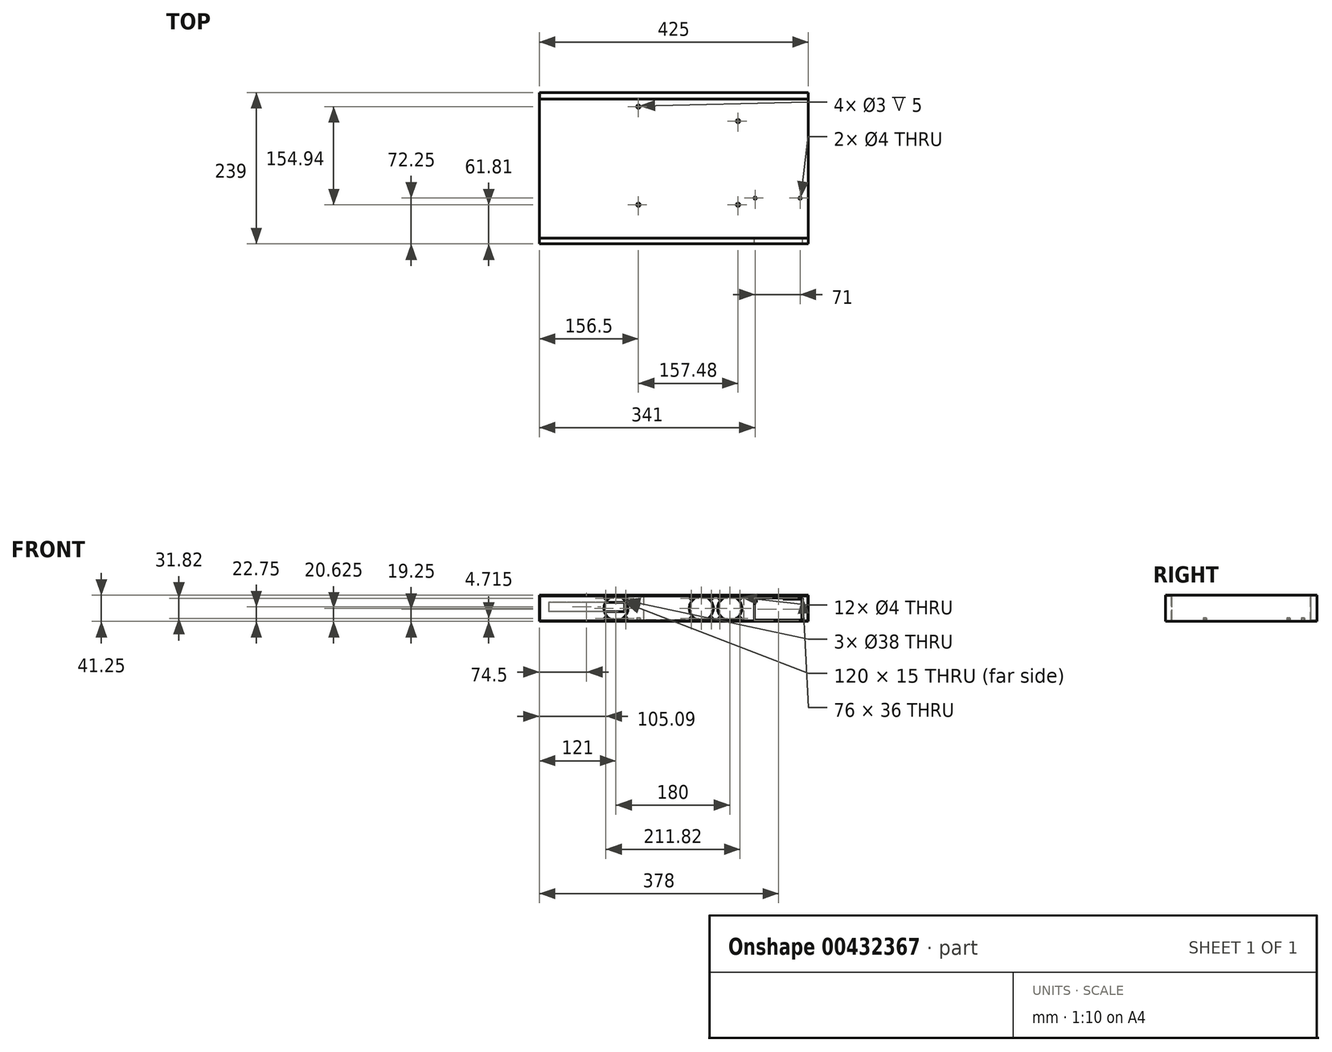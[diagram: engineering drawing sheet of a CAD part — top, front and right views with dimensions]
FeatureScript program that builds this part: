
annotation { "Feature Type Name" : "Feature", "Feature Type Description" : "" }
export const myFeature = defineFeature(function(context is Context, id is Id, definition is map)
    precondition{}
    {
        {
            var Q0;
            Q0=qCreatedBy(makeId("Top.planeOp"),FACE);
            var sketch = newSketch(context, id + "F0", { "sketchPlane" : qUnion([Q0])});
            skLineSegment(sketch, "E0.bottom", {"start": v(0, 219.75) * mm, "end": v(424.5, 219.75) * mm});
            skLineSegment(sketch, "E0.top", {"start": v(0, 0.25) * mm, "end": v(424.5, 0.25) * mm});
            skLineSegment(sketch, "E0.left", {"start": v(0, 219.75) * mm, "end": v(0, 0.25) * mm});
            skLineSegment(sketch, "E0.right", {"start": v(424.5, 219.75) * mm, "end": v(424.5, 0.25) * mm});
            skLineSegment(sketch, "E1.0", {"start": v(-0.25, 220) * mm, "end": v(-0.25, 0) * mm});
            skLineSegment(sketch, "E1.1", {"start": v(-0.25, 220) * mm, "end": v(424.75, 220) * mm});
            skLineSegment(sketch, "E1.2", {"start": v(424.75, 220) * mm, "end": v(424.75, 0) * mm});
            skLineSegment(sketch, "E1.3", {"start": v(-0.25, 0) * mm, "end": v(424.75, 0) * mm});
            skSolve(sketch);
        }
        {
            var Q0;
            Q0=makeQuery(id+"F0.imprint","IMPRINT",FACE,{"disambiguationData":[TD([[makeQuery(id+"F0.imprint","IMPRINT",EDGE,{"derivedFrom":sQuery(id+"F0.wireOp",EDGE,"E0.bottom")}),-1.0]])]});
            var Q1;
            Q1=makeQuery(id+"F0.imprint","IMPRINT",FACE,{"disambiguationData":[TD([[makeQuery(id+"F0.imprint","IMPRINT",EDGE,{"derivedFrom":sQuery(id+"F0.wireOp",EDGE,"E0.bottom")}),1.0]])]});
            extrude(context, id + "F1", {"entities" : qUnion([Q0, Q1]), "oppositeDirection" : true, "depth" : .25 * mm});
        }
        {
            var Q0;
            Q0 = qSketchRegion(id + "F0", true);
            extrude(context, id + "F2", {"entities" : qUnion([Q0]), "operationType" : NewBodyOperationType.ADD, "depth" : 41 * mm});
        }
        {
            var Q0;
            {var subQ0=sQuery(id+"F0.wireOp",EDGE,"E1.3");Q0=makeQuery(id+"F2.boolean.opBoolean","MERGE",FACE,{"derivedFrom":[makeQuery(id+"F1.opExtrude","SWEPT_FACE",FACE,{"disambiguationData":[OSD([subQ0])]}),makeQuery(id+"F2.opExtrude","SWEPT_FACE",FACE,{"disambiguationData":[OSD([subQ0])]})]});}
            var sketch = newSketch(context, id + "F3", { "sketchPlane" : qUnion([Q0])});
            skLineSegment(sketch, "E2", {"start": v(-0.25, 20.37) * mm, "end": v(424.75, 20.38) * mm, "construction": true});
            skCircle(sketch, "E3", {"center": v(120.75, 20.38) * mm, "radius": 19 * mm});
            skCircle(sketch, "E4", {"center": v(255.75, 20.38) * mm, "radius": 19 * mm});
            skCircle(sketch, "E5", {"center": v(300.75, 20.38) * mm, "radius": 19 * mm});
            skLineSegment(sketch, "E6.bottom", {"start": v(339.75, 37) * mm, "end": v(415.75, 37) * mm});
            skLineSegment(sketch, "E6.top", {"start": v(339.75, 1) * mm, "end": v(415.75, 1) * mm});
            skLineSegment(sketch, "E6.left", {"start": v(339.75, 37) * mm, "end": v(339.75, 1) * mm});
            skLineSegment(sketch, "E6.right", {"start": v(415.75, 37) * mm, "end": v(415.75, 1) * mm});
            skCircle(sketch, "E7", {"center": v(104.84, 36.28) * mm, "radius": 2 * mm});
            skLineSegment(sketch, "E8", {"start": v(188.25, 41) * mm, "end": v(188.25, 0) * mm, "construction": true});
            skLineSegment(sketch, "E9", {"start": v(278.25, 41) * mm, "end": v(278.25, 0) * mm, "construction": true});
            skLineSegment(sketch, "E10", {"start": v(104.84, 36.28) * mm, "end": v(120.75, 20.38) * mm, "construction": true});
            skCircle(sketch, "E11.MirrorC", {"center": v(104.84, 4.47) * mm, "radius": 2 * mm});
            skCircle(sketch, "E12.MirrorC", {"center": v(271.66, 36.28) * mm, "radius": 2 * mm});
            skCircle(sketch, "E13.MirrorC", {"center": v(271.66, 4.47) * mm, "radius": 2 * mm});
            skLineSegment(sketch, "E14", {"start": v(120.75, 20.38) * mm, "end": v(120.75, 39.38) * mm, "construction": true});
            skCircle(sketch, "E15.MirrorC", {"center": v(136.66, 36.28) * mm, "radius": 2 * mm});
            skCircle(sketch, "E16.MirrorC", {"center": v(136.66, 4.47) * mm, "radius": 2 * mm});
            skCircle(sketch, "E17.MirrorC", {"center": v(239.84, 36.28) * mm, "radius": 2 * mm});
            skCircle(sketch, "E18.MirrorC", {"center": v(239.84, 4.47) * mm, "radius": 2 * mm});
            skCircle(sketch, "E19.MirrorC", {"center": v(284.84, 36.28) * mm, "radius": 2 * mm});
            skCircle(sketch, "E20.MirrorC", {"center": v(284.84, 4.47) * mm, "radius": 2 * mm});
            skCircle(sketch, "E21.MirrorC", {"center": v(316.66, 36.28) * mm, "radius": 2 * mm});
            skCircle(sketch, "E22.MirrorC", {"center": v(316.66, 4.47) * mm, "radius": 2 * mm});
            skSolve(sketch);
        }
        {
            var Q0;
            {var subQ0=sQuery(id+"F0.wireOp",EDGE,"E1.1");Q0=makeQuery(id+"F2.boolean.opBoolean","MERGE",FACE,{"derivedFrom":[makeQuery(id+"F1.opExtrude","SWEPT_FACE",FACE,{"disambiguationData":[OSD([subQ0])]}),makeQuery(id+"F2.opExtrude","SWEPT_FACE",FACE,{"disambiguationData":[OSD([subQ0])]})]});}
            var sketch = newSketch(context, id + "F4", { "sketchPlane" : qUnion([Q0])});
            skLineSegment(sketch, "E23", {"start": v(-424.75, 20.37) * mm, "end": v(0.25, 20.38) * mm, "construction": true});
            skLineSegment(sketch, "E24.bottom", {"start": v(-414.75, 34.75) * mm, "end": v(-384.75, 34.75) * mm});
            skLineSegment(sketch, "E24.top", {"start": v(-414.75, 1.75) * mm, "end": v(-338.75, 1.75) * mm});
            skLineSegment(sketch, "E24.left", {"start": v(-414.75, 34.75) * mm, "end": v(-414.75, 1.75) * mm});
            skLineSegment(sketch, "E24.right", {"start": v(-338.75, 30) * mm, "end": v(-338.75, 1.75) * mm});
            skLineSegment(sketch, "E25.bottom", {"start": v(-322.25, 40) * mm, "end": v(-164.25, 40) * mm});
            skLineSegment(sketch, "E25.top", {"start": v(-322.25, 1.75) * mm, "end": v(-164.25, 1.75) * mm});
            skLineSegment(sketch, "E25.left", {"start": v(-322.25, 40) * mm, "end": v(-322.25, 1.75) * mm});
            skLineSegment(sketch, "E25.right", {"start": v(-164.25, 40) * mm, "end": v(-164.25, 1.75) * mm});
            skLineSegment(sketch, "E26.bottom", {"start": v(-134.25, 30) * mm, "end": v(-14.25, 30) * mm});
            skLineSegment(sketch, "E26.top", {"start": v(-134.25, 15) * mm, "end": v(-14.25, 15) * mm});
            skLineSegment(sketch, "E26.left", {"start": v(-134.25, 30) * mm, "end": v(-134.25, 15) * mm});
            skLineSegment(sketch, "E26.right", {"start": v(-14.25, 30) * mm, "end": v(-14.25, 15) * mm});
            skLineSegment(sketch, "E27.bottom", {"start": v(-384.75, 40) * mm, "end": v(-342.75, 40) * mm});
            skLineSegment(sketch, "E27.left", {"start": v(-384.75, 40) * mm, "end": v(-384.75, 34.75) * mm});
            skLineSegment(sketch, "E27.right", {"start": v(-342.75, 40) * mm, "end": v(-342.75, 40) * mm});
            skLineSegment(sketch, "E28.top", {"start": v(-342.75, 30) * mm, "end": v(-338.75, 30) * mm});
            skLineSegment(sketch, "E28.left", {"start": v(-342.75, 40) * mm, "end": v(-342.75, 30) * mm});
            skSolve(sketch);
        }
        {
            var Q0;
            Q0 = qSketchRegion(id + "F3", true);
            extrude(context, id + "F5", {"entities" : qUnion([Q0]), "operationType" : NewBodyOperationType.REMOVE, "oppositeDirection" : true, "depth" : 1 * mm});
        }
        {
            var Q0;
            Q0 = qSketchRegion(id + "F4", true);
            extrude(context, id + "F6", {"entities" : qUnion([Q0]), "operationType" : NewBodyOperationType.REMOVE, "oppositeDirection" : true, "depth" : 1 * mm});
        }
        {
            var Q0;
            {var subQ0=sQuery(id+"F0.wireOp",EDGE,"E1.3");Q0=makeQuery(id+"F2.boolean.opBoolean","MERGE",FACE,{"derivedFrom":[makeQuery(id+"F1.opExtrude","SWEPT_FACE",FACE,{"disambiguationData":[OSD([subQ0])]}),makeQuery(id+"F2.opExtrude","SWEPT_FACE",FACE,{"disambiguationData":[OSD([subQ0])]})]});}
            var sketch = newSketch(context, id + "F7", { "sketchPlane" : qUnion([Q0])});
            skLineSegment(sketch, "E29.bottom", {"start": v(-0.25, 41) * mm, "end": v(424.75, 41) * mm});
            skLineSegment(sketch, "E29.top", {"start": v(-0.25, -0.25) * mm, "end": v(339.75, -0.25) * mm});
            skLineSegment(sketch, "E29.left", {"start": v(-0.25, 41) * mm, "end": v(-0.25, -0.25) * mm});
            skLineSegment(sketch, "E29.right", {"start": v(424.75, 41) * mm, "end": v(424.75, -0.25) * mm});
            skLineSegment(sketch, "E30.0", {"start": v(0.75, 40) * mm, "end": v(0.75, 0.75) * mm});
            skLineSegment(sketch, "E30.1", {"start": v(0.75, 40) * mm, "end": v(423.75, 40) * mm});
            skLineSegment(sketch, "E30.2", {"start": v(423.75, 40) * mm, "end": v(423.75, 0.75) * mm});
            skLineSegment(sketch, "E30.3", {"start": v(0.75, 0.75) * mm, "end": v(339.75, 0.75) * mm});
            skLineSegment(sketch, "E31", {"start": v(339.75, 0.75) * mm, "end": v(339.75, -0.25) * mm});
            skLineSegment(sketch, "E32", {"start": v(415.75, 0.75) * mm, "end": v(415.75, -0.25) * mm});
            skLineSegment(sketch, "E33.trimOffspring", {"start": v(415.75, 0.75) * mm, "end": v(423.75, 0.75) * mm});
            skLineSegment(sketch, "E34.trimOffspring", {"start": v(415.75, -0.25) * mm, "end": v(424.75, -0.25) * mm});
            skSolve(sketch);
        }
        {
            var Q0;
            Q0 = qSketchRegion(id + "F7", true);
            extrude(context, id + "F8", {"entities" : qUnion([Q0]), "operationType" : NewBodyOperationType.ADD, "depth" : 9 * mm});
        }
        {
            var Q0;
            Q0=makeQuery(id+"F5.boolean.opBoolean","MERGE",FACE,{"derivedFrom":[makeQuery(id+"F1.opExtrude","CAP_FACE",FACE,{"disambiguationData":[OSD([sQuery(id+"F0.wireOp",EDGE,"E1.0"),sQuery(id+"F0.wireOp",EDGE,"E1.1"),sQuery(id+"F0.wireOp",EDGE,"E1.2"),sQuery(id+"F0.wireOp",EDGE,"E1.3")])],"isStart":true}),makeQuery(id+"F5.opExtrude","SWEPT_FACE",FACE,{"disambiguationData":[OSD([sQuery(id+"F3.wireOp",EDGE,"E6.top")])]})]});
            var sketch = newSketch(context, id + "F9", { "sketchPlane" : qUnion([Q0])});
            skCircle(sketch, "E35", {"center": v(156.25, 207.75) * mm, "radius": 2.75 * mm});
            skCircle(sketch, "E36", {"center": v(313.73, 184.9) * mm, "radius": 2.75 * mm});
            skLineSegment(sketch, "E37", {"start": v(243.25, 219.75) * mm, "end": v(243.25, 0.25) * mm, "construction": true});
            skCircle(sketch, "E38", {"center": v(156.25, 207.75) * mm, "radius": 1.5 * mm});
            skCircle(sketch, "E39", {"center": v(313.73, 184.9) * mm, "radius": 1.5 * mm});
            skCircle(sketch, "E40", {"center": v(156.25, 52.81) * mm, "radius": 2.75 * mm});
            skCircle(sketch, "E41", {"center": v(156.25, 52.81) * mm, "radius": 1.5 * mm});
            skCircle(sketch, "E42.MirrorC", {"center": v(313.73, 52.81) * mm, "radius": 2.75 * mm});
            skCircle(sketch, "E43.MirrorC", {"center": v(313.73, 52.81) * mm, "radius": 1.5 * mm});
            skLineSegment(sketch, "E44", {"start": v(156.25, 207.75) * mm, "end": v(243.25, 207.75) * mm, "construction": true});
            skSolve(sketch);
        }
        {
            var Q0;
            Q0 = qSketchRegion(id + "F9", true);
            extrude(context, id + "F10", {"entities" : qUnion([Q0]), "operationType" : NewBodyOperationType.ADD, "depth" : 5 * mm});
        }
        {
            var Q0;
            {var subQ0=sQuery(id+"F0.wireOp",EDGE,"E1.1");Q0=makeQuery(id+"F2.boolean.opBoolean","MERGE",FACE,{"derivedFrom":[makeQuery(id+"F1.opExtrude","SWEPT_FACE",FACE,{"disambiguationData":[OSD([subQ0])]}),makeQuery(id+"F2.opExtrude","SWEPT_FACE",FACE,{"disambiguationData":[OSD([subQ0])]})]});}
            var sketch = newSketch(context, id + "F11", { "sketchPlane" : qUnion([Q0])});
            skLineSegment(sketch, "E45.bottom", {"start": v(-424.75, 41) * mm, "end": v(0, 41) * mm});
            skLineSegment(sketch, "E45.top", {"start": v(-424.75, 0) * mm, "end": v(0, 0) * mm});
            skLineSegment(sketch, "E45.left", {"start": v(-424.75, 41) * mm, "end": v(-424.75, 0) * mm});
            skLineSegment(sketch, "E45.right", {"start": v(0, 41) * mm, "end": v(0, 0) * mm});
            skLineSegment(sketch, "E46.0", {"start": v(-423.75, 40) * mm, "end": v(-423.75, 1) * mm});
            skLineSegment(sketch, "E46.1", {"start": v(-423.75, 40) * mm, "end": v(-1, 40) * mm});
            skLineSegment(sketch, "E46.2", {"start": v(-1, 40) * mm, "end": v(-1, 1) * mm});
            skLineSegment(sketch, "E46.3", {"start": v(-423.75, 1) * mm, "end": v(-1, 1) * mm});
            skSolve(sketch);
        }
        {
            var Q0;
            Q0 = qSketchRegion(id + "F11", true);
            extrude(context, id + "F12", {"entities" : qUnion([Q0]), "operationType" : NewBodyOperationType.ADD, "depth" : 10 * mm});
        }
        {
            var Q0;
            Q0=makeQuery(id+"F10.boolean.opBoolean","SPLIT",FACE,{"disambiguationData":[TD([makeQuery(id+"F2.opExtrude","SWEPT_FACE",FACE,{"disambiguationData":[OSD([sQuery(id+"F0.wireOp",EDGE,"E0.bottom")])]})])],"derivedFrom":makeQuery(id+"F1.opExtrude","CAP_FACE",FACE,{"disambiguationData":[OSD([sQuery(id+"F0.wireOp",EDGE,"E1.0"),sQuery(id+"F0.wireOp",EDGE,"E1.1"),sQuery(id+"F0.wireOp",EDGE,"E1.2"),sQuery(id+"F0.wireOp",EDGE,"E1.3")])],"isStart":true})});
            var sketch = newSketch(context, id + "F13", { "sketchPlane" : qUnion([Q0])});
            skCircle(sketch, "E47", {"center": v(340.75, 63.25) * mm, "radius": 2 * mm});
            skCircle(sketch, "E48", {"center": v(411.75, 63.25) * mm, "radius": 2 * mm});
            skSolve(sketch);
        }
        {
            var Q0;
            Q0 = qSketchRegion(id + "F13", true);
            extrude(context, id + "F14", {"entities" : qUnion([Q0]), "operationType" : NewBodyOperationType.REMOVE, "endBound" : BoundingType.UP_TO_NEXT, "oppositeDirection" : true, "depth" : 25 * mm});
        }
    });
